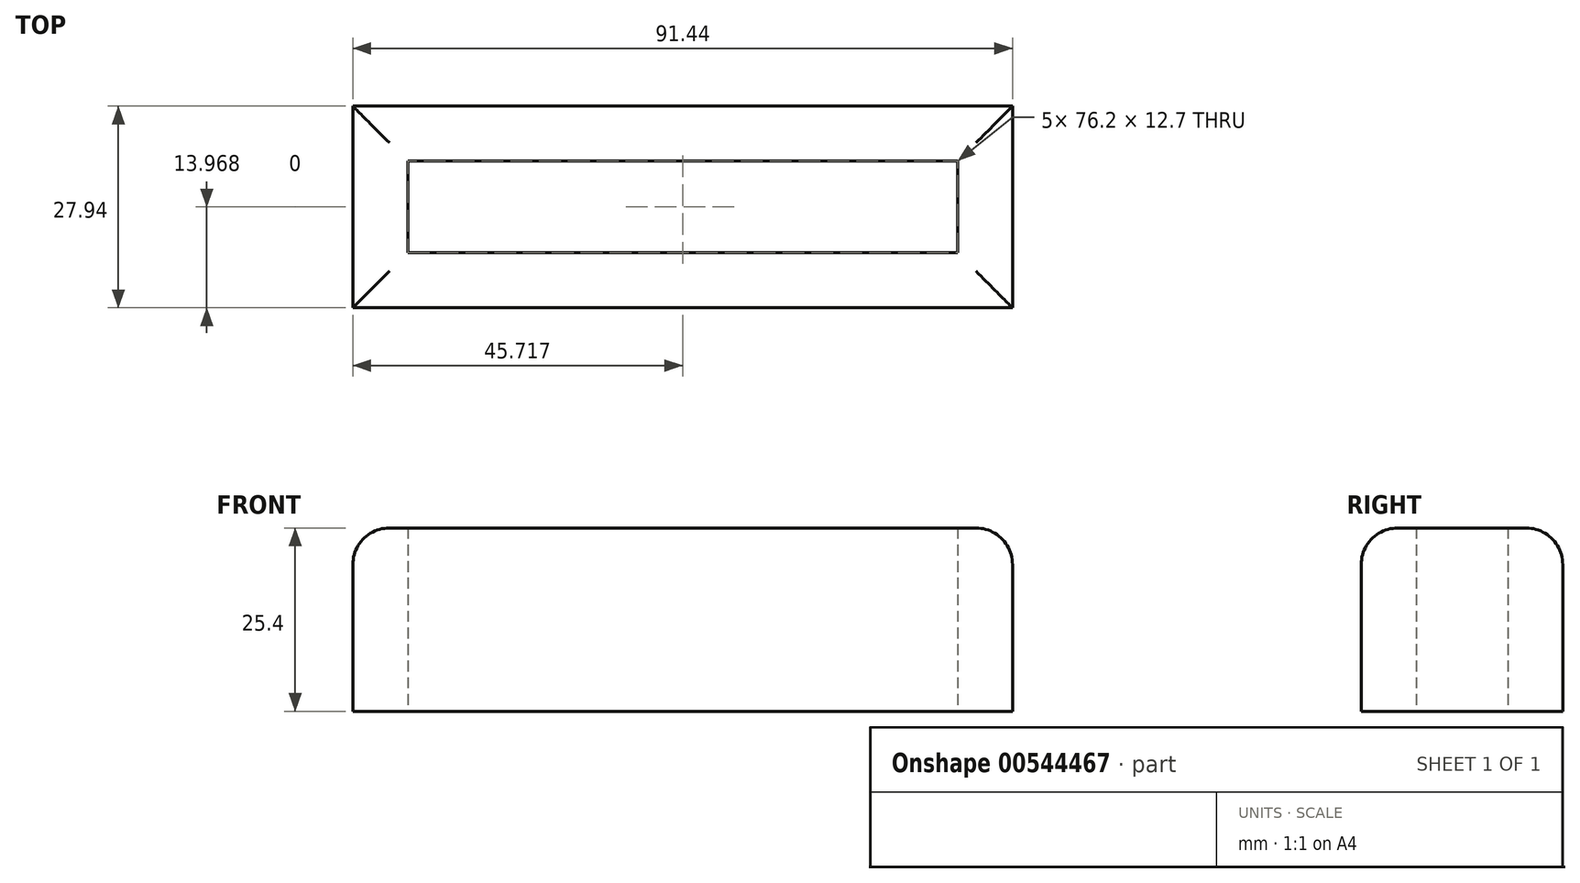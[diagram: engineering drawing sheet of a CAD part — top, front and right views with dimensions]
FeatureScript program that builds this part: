
annotation { "Feature Type Name" : "Feature", "Feature Type Description" : "" }
export const myFeature = defineFeature(function(context is Context, id is Id, definition is map)
    precondition{}
    {
        {
            var Q0;
            Q0=qCreatedBy(makeId("Top.planeOp"),FACE);
            var sketch = newSketch(context, id + "F0", { "sketchPlane" : qUnion([Q0])});
            skLineSegment(sketch, "E0.bottom", {"start": v(-22.47, -2.6) * mm, "end": v(53.73, -2.6) * mm});
            skLineSegment(sketch, "E0.top", {"start": v(-22.47, -15.3) * mm, "end": v(53.73, -15.3) * mm});
            skLineSegment(sketch, "E0.left", {"start": v(-22.47, -2.6) * mm, "end": v(-22.47, -15.3) * mm});
            skLineSegment(sketch, "E0.right", {"start": v(53.73, -2.6) * mm, "end": v(53.73, -15.3) * mm});
            skLineSegment(sketch, "E1.0", {"start": v(-30.1, 5.02) * mm, "end": v(61.35, 5.02) * mm});
            skLineSegment(sketch, "E1.1", {"start": v(-30.1, 5.02) * mm, "end": v(-30.1, -22.92) * mm});
            skLineSegment(sketch, "E1.2", {"start": v(-30.1, -22.92) * mm, "end": v(61.35, -22.92) * mm});
            skLineSegment(sketch, "E1.3", {"start": v(61.35, 5.02) * mm, "end": v(61.35, -22.92) * mm});
            skSolve(sketch);
        }
        {
            var Q0;
            Q0 = qSketchRegion(id + "F0", true);
            extrude(context, id + "F1", {"entities" : qUnion([Q0]), "depth" : 25.4 * mm, "offsetDistance" : 25.4 * mm});
        }
        {
            var Q0;
            Q0=makeQuery(id+"F1.opExtrude","CAP_EDGE",EDGE,{"disambiguationData":[OSD([sQuery(id+"F0.wireOp",EDGE,"E1.2")])],"isStart":false});
            var Q1;
            Q1=makeQuery(id+"F1.opExtrude","CAP_EDGE",EDGE,{"disambiguationData":[OSD([sQuery(id+"F0.wireOp",EDGE,"E1.1")])],"isStart":false});
            var Q2;
            Q2=makeQuery(id+"F1.opExtrude","CAP_EDGE",EDGE,{"disambiguationData":[OSD([sQuery(id+"F0.wireOp",EDGE,"E1.3")])],"isStart":false});
            var Q3;
            Q3=makeQuery(id+"F1.opExtrude","CAP_EDGE",EDGE,{"disambiguationData":[OSD([sQuery(id+"F0.wireOp",EDGE,"E1.0")])],"isStart":false});
            fillet(context, id + "F2", {"entities" : qUnion([Q0, Q1, Q2, Q3]), "radius" : 5.08 * mm, "tangentPropagation" : true, "allowEdgeOverflow" : false});
        }
    });
